# Revit family: 707220001_Fluxometro Orinal Palanca
name_source: partatom
category: Generic Models
units: mm (PartAtom-declared; Revit-internal decimal feet)

## family parameters
Always vertical = Yes
Can host rebar = No
Cut with Voids When Loaded = No
Part Type = Normal
Room Calculation Point = No
Round Connector Dimension = Use Diameter
Shared = No
Work Plane-Based = No

## types (1)
- 707220001_Fluxometro Orinal Palanca
    Acabado = Corona_Cromado
    Accionamiento mediante = Palanca
    Capacidad de Flujo estimado real = 0,48 L/min a 50 PSI
    Ciclo de Vida y Desempeño de la descarga = 150,000 ciclos
    Consumo = 0,5 Lpf. - 0,125 Gpf
    Creado por = IDD
    Descarga Por = Pistón
    Description = El Fluxómetro para Orinal de Corona, te garantizará un ahorro de agua en cada descarga consumiendo 0.5 lpf, haciéndolo ideal para instituciones de alto tráfico. ¡Tienes que tenerlo!
    Diametro de Tubería para la instalación = Entrada Mínimo de 1/2 y/o 3/4 NPT, Salida de 3/4 Tuerca de 3/4 para conexión a Racor de 3/4.
e descarga total: 0,48 L/min a 50 PSI
    Dimensiónes generales de producto (H x W x L) = 329 x 85 x 291 mm.
    Fecha de creación = 5/10/2020
    Material = Corona_Cromado
    Peso Bruto Aproximado = 2,320 gr. 5,1147 lb
    Peso Neto Aproximado = 2,080 gr. 4,5856 lb
    Presión máxima recomendada = 80 psi
    Presión mínima recomendada = 20 psi
    Ruptor de vacioi = Si
    Tipo de instalación = Expuesto E.S.
    URL = https://corona.co

## geometry (parser evidence)
native form markers: Sweep x2
no freeform markers — native parametric forms only
